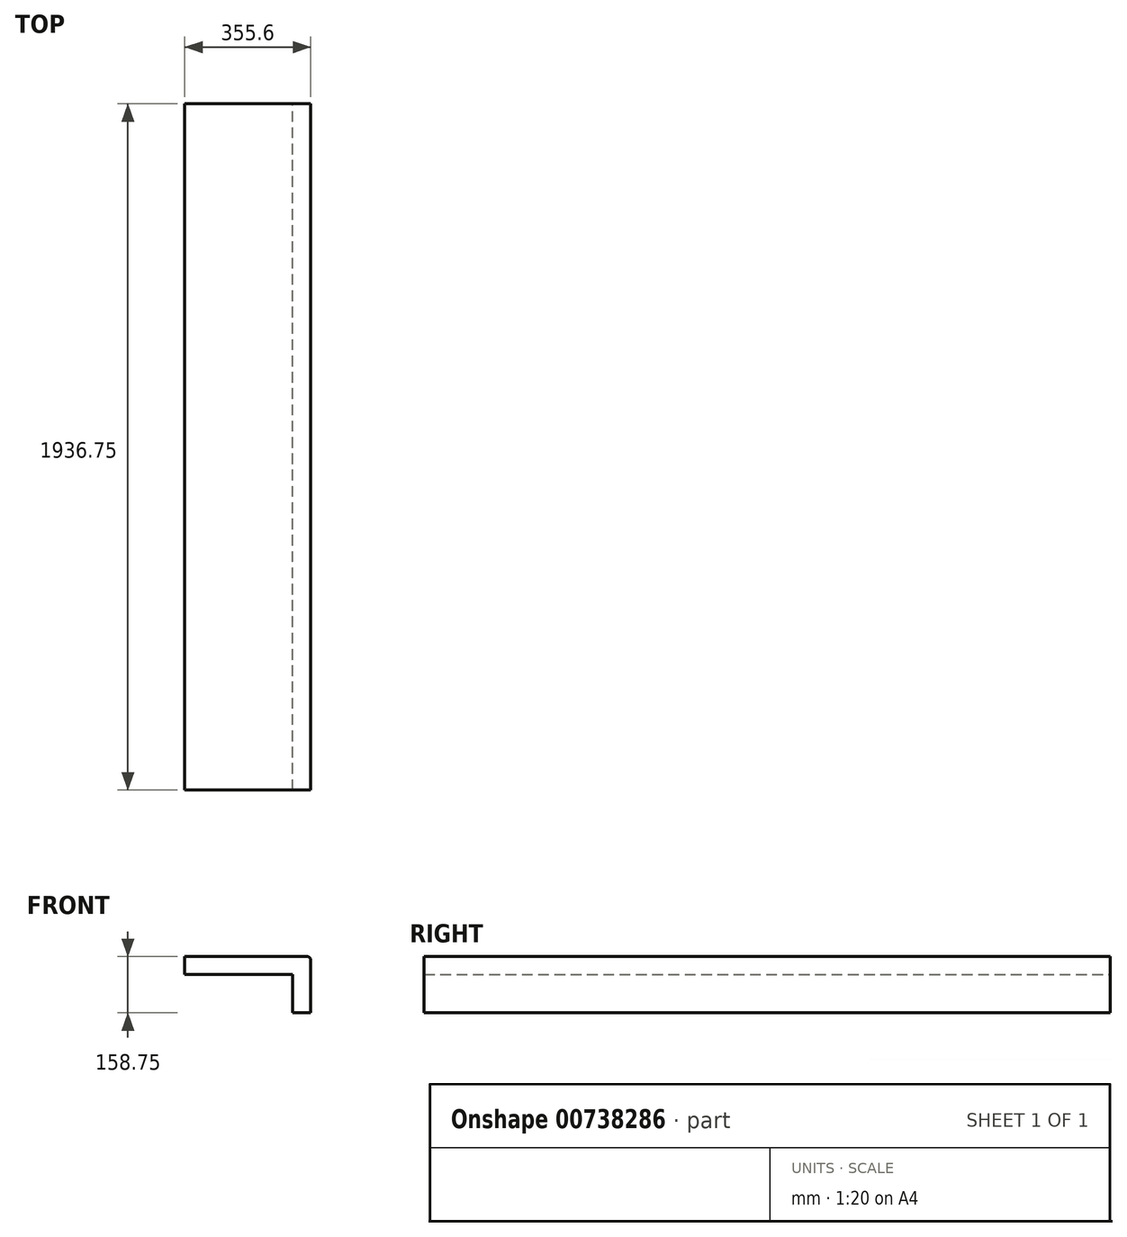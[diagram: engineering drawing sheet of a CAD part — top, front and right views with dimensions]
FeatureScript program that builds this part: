
annotation { "Feature Type Name" : "Feature", "Feature Type Description" : "" }
export const myFeature = defineFeature(function(context is Context, id is Id, definition is map)
    precondition{}
    {
        {
            var Q0;
            Q0=qCreatedBy(makeId("Front.planeOp"),FACE);
            var sketch = newSketch(context, id + "F0", { "sketchPlane" : qUnion([Q0])});
            skLineSegment(sketch, "E0", {"start": v(45.8, -8.15) * mm, "end": v(45.8, 99.8) * mm});
            skLineSegment(sketch, "E1", {"start": v(45.8, 99.8) * mm, "end": v(-259, 99.8) * mm});
            skLineSegment(sketch, "E2", {"start": v(-259, 99.8) * mm, "end": v(-259, 150.6) * mm});
            skLineSegment(sketch, "E3", {"start": v(45.8, -8.15) * mm, "end": v(96.6, -8.15) * mm});
            skLineSegment(sketch, "E4", {"start": v(-259, 150.6) * mm, "end": v(87.07, 150.6) * mm});
            skLineSegment(sketch, "E5", {"start": v(96.6, 141.07) * mm, "end": v(96.6, -8.15) * mm});
            skPoint(sketch, "E6.visualSharp", {"position": v(96.6, 150.6) * mm});
            skArc(sketch, "E6.filletArc", {"start": v(96.6, 141.07) * mm, "mid": v(93.8, 147.8) * mm, "end": v(87.07, 150.6) * mm});
            skSolve(sketch);
        }
        {
            var Q0;
            Q0 = qSketchRegion(id + "F0", true);
            extrude(context, id + "F1", {"entities" : qUnion([Q0]), "depth" : 1936.75 * mm, "offsetDistance" : 25.4 * mm});
        }
    });
